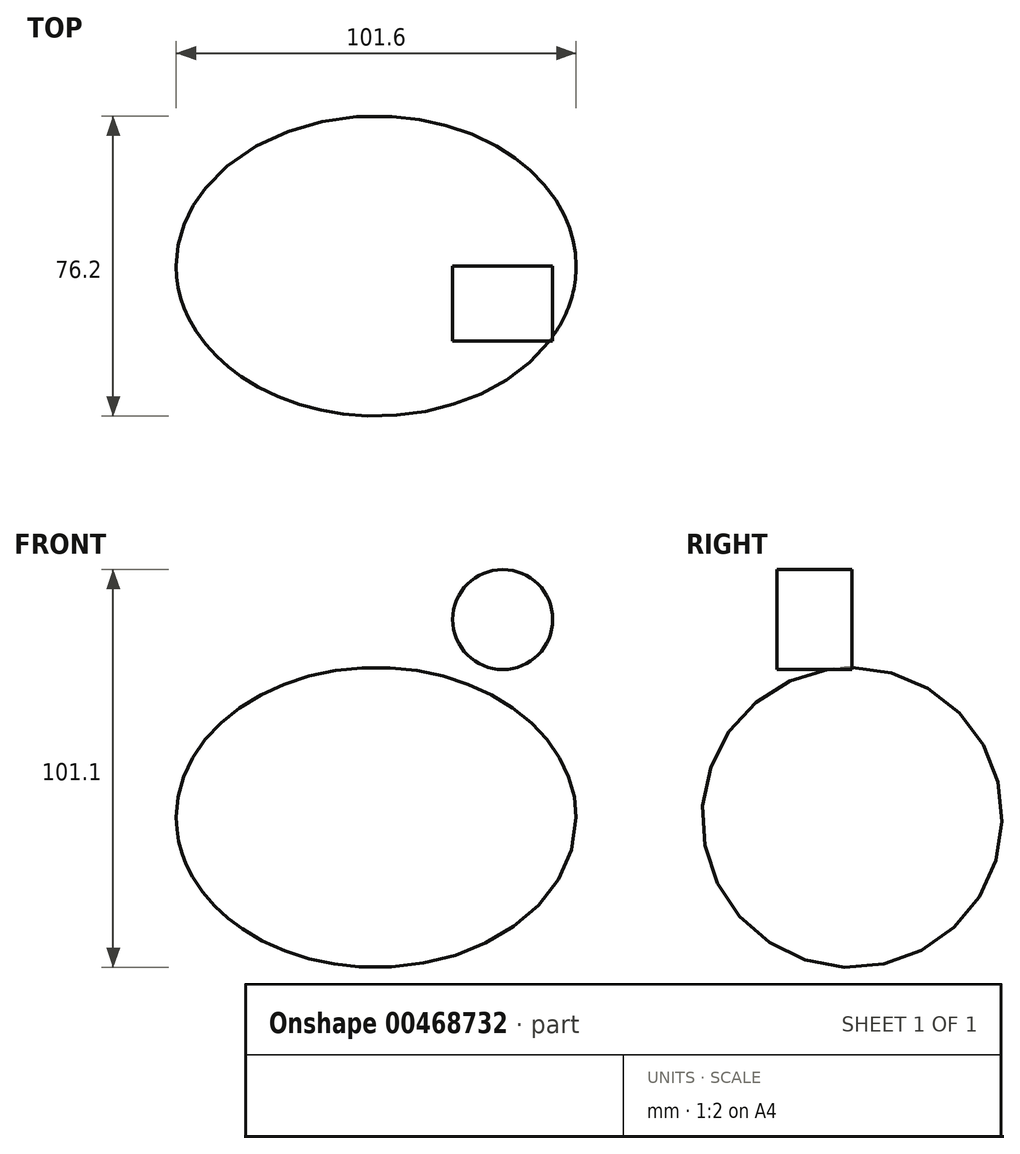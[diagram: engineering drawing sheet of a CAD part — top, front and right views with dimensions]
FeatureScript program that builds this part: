
annotation { "Feature Type Name" : "Feature", "Feature Type Description" : "" }
export const myFeature = defineFeature(function(context is Context, id is Id, definition is map)
    precondition{}
    {
        {
            var Q0;
            Q0=qCreatedBy(makeId("Front.planeOp"),FACE);
            var sketch = newSketch(context, id + "F0", { "sketchPlane" : qUnion([Q0])});
            skEllipticalArc(sketch, "E0", {});
            skLineSegment(sketch, "E1", {"start": v(-50.8, 0) * mm, "end": v(50.8, 0) * mm});
            skLineSegment(sketch, "E2", {"start": v(-75.83, 38.1) * mm, "end": v(78, 38.1) * mm, "construction": true});
            const initialGuessF0  = {"E0": [0, 0, 1, 0, 0.0508, 0.0381, 0, 3.141592653589793]};
            skSetInitialGuess(sketch, initialGuessF0);
            skSolve(sketch);
        }
        {
            var Q0;
            Q0=makeQuery(id+"F0.imprint","IMPRINT",FACE,{"disambiguationData":[TD([[makeQuery(id+"F0.imprint","IMPRINT",EDGE,{"derivedFrom":sQuery(id+"F0.wireOp",EDGE,"E0")}),1.0]])]});
            var Q1;
            Q1=sQuery(id+"F0.wireOp",EDGE,"E1");
            revolve(context, id + "F1", {"entities" : qUnion([Q0]), "axis" : qUnion([Q1]), "revolveType" : RevolveType.FULL});
        }
        {
            var Q0;
            Q0=qCreatedBy(makeId("Front.planeOp"),FACE);
            var sketch = newSketch(context, id + "F2", { "sketchPlane" : qUnion([Q0])});
            skCircle(sketch, "E3", {"center": v(32.16, 50.3) * mm, "radius": 12.7 * mm});
            skSolve(sketch);
        }
        {
            var Q0;
            Q0=makeQuery(id+"F2.imprint","IMPRINT",FACE,{"disambiguationData":[TD([[makeQuery(id+"F2.imprint","IMPRINT",EDGE,{"derivedFrom":sQuery(id+"F2.wireOp",EDGE,"E3")}),1.0]])]});
            extrude(context, id + "F3", {"entities" : qUnion([Q0]), "depth" : 19.05 * mm});
        }
        {
            var Q0;
            Q0=makeQuery(id+"F3.opExtrude","SWEPT_BODY",BODY,{"disambiguationData":[OSD([sQuery(id+"F2.wireOp",EDGE,"E3")])]});
            transform(context, id + "F4", {"entities" : qUnion([Q0]), "transformType" : TransformType.TRANSLATION_3D, "dx" : 48.5 * mm, "dy" : 0 * mm, "dz" : 0 * mm, "makeCopy" : true});
        }
        {
            var Q0;
            Q0=makeQuery(id+"F4.opPattern","COPY",BODY,{"derivedFrom":makeQuery(id+"F3.opExtrude","SWEPT_BODY",BODY,{"disambiguationData":[OSD([sQuery(id+"F2.wireOp",EDGE,"E3")])]}),"instanceName":"1"});
            deleteBodies(context, id + "F5", {"entities" : qUnion([Q0])});
        }
    });
